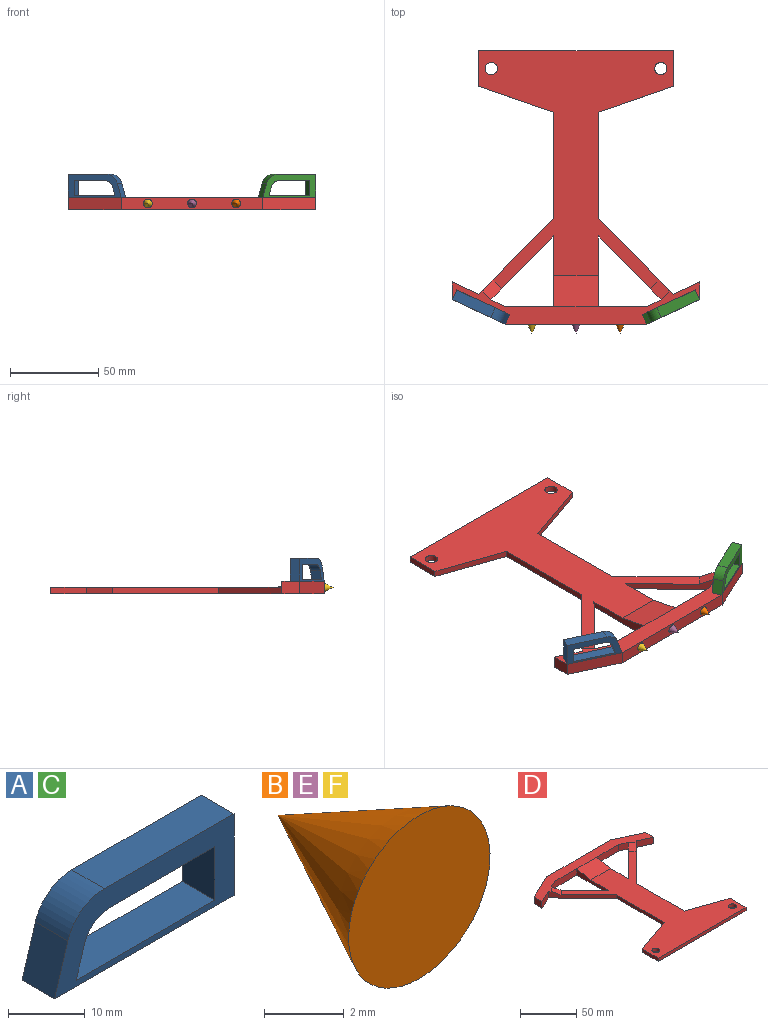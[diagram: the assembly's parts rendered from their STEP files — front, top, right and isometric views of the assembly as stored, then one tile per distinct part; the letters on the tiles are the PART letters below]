
ASSEMBLY  parts=6 mates=5
PART A: 12 faces, bbox 33x6x13 mm
  f0: plane 25.54x6mm, normal (0,0,1), area 153.2mm2, adj f1,f7,f8,f9
  f1: plane 6x4.96mm, normal (0.96,0,-0.29), area 31.1mm2, adj f0,f8,f9,f11
  f2: plane 19.24x6mm, normal (0,0,-1), area 115.4mm2, adj f7,f8,f9,f11
  f3: plane 8.04x6mm, normal (-0.96,0,0.29), area 50.4mm2, adj f4,f8,f9,f10
  f4: plane 33x6mm, normal (0,0,-1), area 198mm2, adj f3,f5,f8,f9
  f5: plane 13x6mm, normal (1,0,0), area 78mm2, adj f4,f6,f8,f9
  f6: plane 23.85x6mm, normal (0,0,1), area 143.1mm2, adj f5,f8,f9,f10
  f7: plane 8.5x6mm, normal (-1,0,0), area 51mm2, adj f0,f2,f8,f9
  f8: plane 33x13mm, normal (0,-1,0), area 194.7mm2, adj f0,f1,f2,f3,f4,f5,f6,f7
  f9: plane 33x13mm, normal (0,1,0), area 194.7mm2, adj f0,f1,f2,f3,f4,f5,f6,f7
  f10: cylinder r=7mm len=6.7mm, axis (0,1,0), area 53.5mm2, adj f3,f6,f8,f9
  f11: cylinder r=5mm len=6mm, axis (0,-1,0), area 38.2mm2, adj f1,f2,f8,f9
PART B: 2 faces, bbox 5x5x5 mm
  f0: plane 5x5mm, normal (0,-1,0), area 19.6mm2, adj f1
  f1: cone r=0mm half-angle=26.6deg, axis (0,-1,0), area 43.9mm2, adj f0
PART C: same geometry as A
PART D: 32 faces, bbox 140x154.8x7 mm
  f0: plane 134.72x110mm, normal (0,0,1), area 6072.8mm2, adj f1,f2,f3,f4,f5,f6,f7,f8
  f1: plane 60.05x3.5mm, normal (1,0,0), area 210.2mm2, adj f0,f2,f15,f16
  f2: plane 42.96x42.5mm, normal (0.71,-0.7,0), area 235.6mm2, adj f0,f1,f16,f22,f28,f30
  f3: plane 36.15x35.76mm, normal (-0.71,0.7,0), area 193.3mm2, adj f0,f4,f16,f21,f30
  f4: plane 40x7mm, normal (1,0,0), area 170.6mm2, adj f0,f3,f16,f20,f29
  f5: plane 40x7mm, normal (-1,0,0), area 170.6mm2, adj f0,f6,f16,f19,f29
  f6: plane 36.15x35.76mm, normal (0.71,0.7,0), area 193.3mm2, adj f0,f5,f16,f18,f31
  f7: plane 42.96x42.5mm, normal (-0.71,-0.7,0), area 235.6mm2, adj f0,f8,f16,f17,f28,f31
  f8: plane 60.05x3.5mm, normal (-1,0,0), area 210.2mm2, adj f0,f7,f9,f16
  f9: plane 42.5x14.79mm, normal (-0.33,0.94,0), area 157.5mm2, adj f0,f8,f10,f16
  f10: plane 20x3.5mm, normal (-1,0,0), area 70mm2, adj f0,f9,f11,f16
  f11: plane 110x3.5mm, normal (0,-1,0), area 385mm2, adj f0,f10,f12,f16
  f12: plane 20x3.5mm, normal (1,0,0), area 70mm2, adj f0,f11,f15,f16
  f13: cylinder r=3.5mm len=7mm, axis (0,0,-1), area 77mm2, adj f0,f16
  f14: cylinder r=3.5mm len=7mm, axis (0,0,-1), area 77mm2, adj f0,f16
  f15: plane 42.5x14.79mm, normal (0.33,0.94,0), area 157.5mm2, adj f0,f1,f12,f16
  f16: plane 154.79x140mm, normal (0,0,-1), area 8050.3mm2, adj f1,f2,f3,f4,f5,f6,f7,f8
  f17: plane 15x7mm, normal (0.42,-0.91,0), area 115.9mm2, adj f7,f16,f27,f28
  f18: plane 8.26x7mm, normal (0.42,-0.91,0), area 63.8mm2, adj f6,f16,f19,f28
  f19: plane 27.5x7mm, normal (0,-1,0), area 192.5mm2, adj f5,f16,f18,f28
  f20: plane 27.5x7mm, normal (0,-1,0), area 192.5mm2, adj f4,f16,f21,f28
  f21: plane 8.26x7mm, normal (-0.42,-0.91,0), area 63.8mm2, adj f3,f16,f20,f28
  f22: plane 15x7mm, normal (-0.42,-0.91,0), area 115.9mm2, adj f2,f16,f23,f28
  f23: plane 10x7mm, normal (1,0,0), area 70mm2, adj f16,f22,f24,f28
  f24: plane 30x13.99mm, normal (0.42,0.91,0), area 231.7mm2, adj f16,f23,f25,f28
  f25: plane 80x7mm, normal (0,1,0), area 560mm2, adj f16,f24,f26,f28
  f26: plane 30x13.99mm, normal (-0.42,0.91,0), area 231.7mm2, adj f16,f25,f27,f28
  f27: plane 10x7mm, normal (-1,0,0), area 70mm2, adj f16,f17,f26,f28
  f28: plane 140x23.99mm, normal (0,0,1), area 1417.5mm2, adj f2,f7,f17,f18,f19,f20,f21,f22
  f29: plane 25x17.5mm, normal (0,-0.2,0.98), area 446.2mm2, adj f0,f4,f5,f28
  f30: plane 11.14x11.13mm, normal (-0.26,-0.26,0.93), area 66mm2, adj f0,f2,f3,f28
  f31: plane 11.14x11.13mm, normal (0.26,-0.26,0.93), area 66mm2, adj f0,f6,f7,f28
PART E: same geometry as B
PART F: same geometry as B
PLACE A rot(axis=(0,0,1),155deg) t=(-95.05,-154.77,7)mm
PLACE B rot(axis=(0,0,-1),180deg) t=(-30,-154.79,3.5)mm
PLACE C rot(axis=(0,0,1),25deg) t=(-17.49,-149.33,7)mm
PLACE D rot(axis=(0,0,-1),180deg) t=(0,0,0)mm
PLACE E rot(axis=(0,0,-1),180deg) t=(-55,-154.79,3.5)mm
PLACE F rot(axis=(0,0,-1),180deg) t=(-80,-154.79,3.5)mm
MATE revolute A.f4 <-> D.f28  axis (0,0,-1) through (-110,-147.8,7)mm
MATE fastened D.f25 <-> E.f1  axis (0,-1,0) through (-55,-154.79,3.5)mm
MATE parallel A.f9 <-> D.f24  axis (-0.42,-0.91,0) through (-121.78,-142.3,8)mm
MATE revolute D.f28 <-> C.f4  axis (0,0,1) through (0,-147.8,7)mm
MATE parallel C.f8 <-> D.f26  axis (0.42,-0.91,0) through (11.78,-142.3,8)mm
